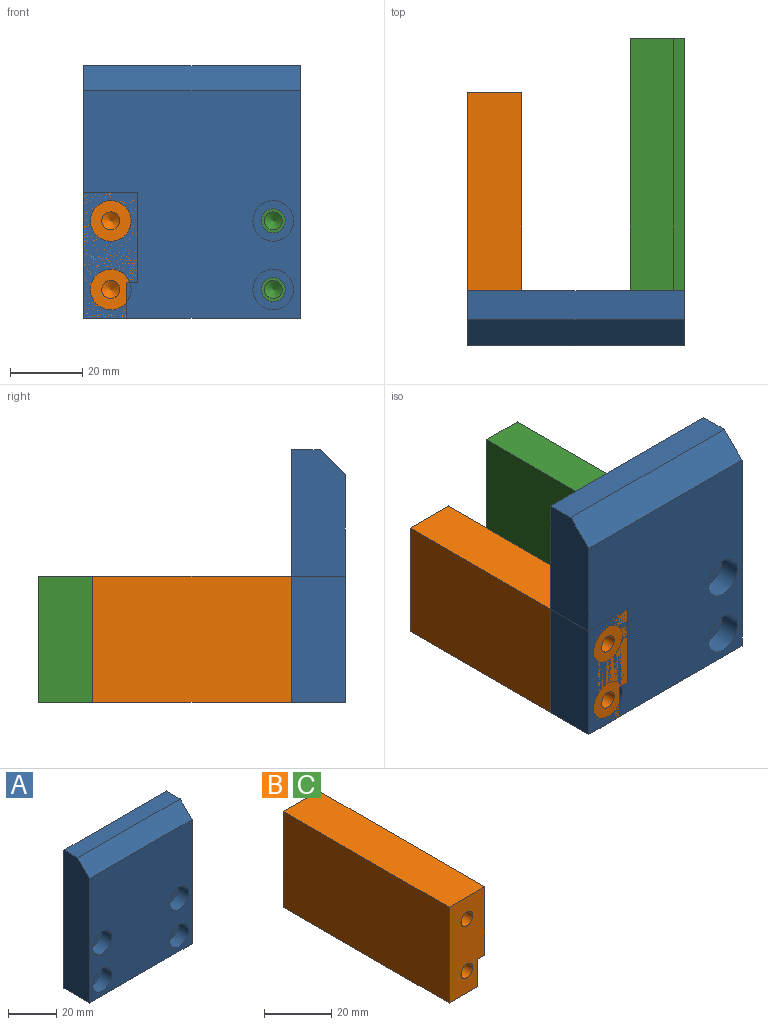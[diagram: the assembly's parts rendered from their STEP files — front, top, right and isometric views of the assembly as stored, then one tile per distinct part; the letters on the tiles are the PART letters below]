
ASSEMBLY  parts=3 mates=4
PART A: 19 faces, bbox 60x15x70 mm
  f0: plane 70x15mm, normal (-1,0,0), area 1025.5mm2, adj f1,f3,f4,f5,f6
  f1: plane 60x15mm, normal (0,0,-1), area 900mm2, adj f0,f2,f4,f5
  f2: plane 70x15mm, normal (1,0,0), area 1025.5mm2, adj f1,f3,f4,f5,f6
  f3: plane 60x8mm, normal (0,0,1), area 480mm2, adj f0,f2,f4,f6
  f4: plane 70x60mm, normal (0,1,0), area 4063.2mm2, adj f0,f1,f2,f3,f7,f10,f13,f16
  f5: plane 63x60mm, normal (0,-1,0), area 3382.4mm2, adj f0,f1,f2,f6,f9,f12,f15,f18
  f6: plane 60x7mm, normal (0,-0.71,0.71), area 594mm2, adj f0,f2,f3,f5
  f7: cylinder r=3.3mm len=9mm, axis (0,-1,0), area 186.6mm2, adj f4,f8
  f8: plane 11.25x11.25mm, normal (0,-1,0), area 65.2mm2, adj f7,f9
  f9: cylinder r=5.62mm len=11.25mm, axis (0,-1,0), area 212.1mm2, adj f5,f8
  f10: cylinder r=3.3mm len=9mm, axis (0,-1,0), area 186.6mm2, adj f4,f11
  f11: plane 11.25x11.25mm, normal (0,-1,0), area 65.2mm2, adj f10,f12
  f12: cylinder r=5.62mm len=11.25mm, axis (0,-1,0), area 212.1mm2, adj f5,f11
  f13: cylinder r=3.3mm len=9mm, axis (0,-1,0), area 186.6mm2, adj f4,f14
  f14: plane 11.25x11.25mm, normal (0,-1,0), area 65.2mm2, adj f13,f15
  f15: cylinder r=5.62mm len=11.25mm, axis (0,-1,0), area 212.1mm2, adj f5,f14
  f16: cylinder r=3.3mm len=9mm, axis (0,-1,0), area 186.6mm2, adj f4,f17
  f17: plane 11.25x11.25mm, normal (0,-1,0), area 65.2mm2, adj f16,f18
  f18: cylinder r=5.62mm len=11.25mm, axis (0,-1,0), area 212.1mm2, adj f5,f17
PART B: 16 faces, bbox 15x70x35 mm
  f0: plane 70x35mm, normal (-1,0,0), area 2450mm2, adj f1,f5,f6,f7
  f1: plane 70x12mm, normal (0,0,-1), area 840mm2, adj f0,f2,f6,f7
  f2: plane 70x10mm, normal (1,0,0), area 700mm2, adj f1,f3,f6,f7
  f3: plane 70x3mm, normal (0,0,-1), area 210mm2, adj f2,f4,f6,f7
  f4: plane 70x25mm, normal (1,0,0), area 1750mm2, adj f3,f5,f6,f7
  f5: plane 70x15mm, normal (0,0,1), area 1050mm2, adj f0,f4,f6,f7
  f6: plane 35x15mm, normal (0,1,0), area 455.7mm2, adj f0,f1,f2,f3,f4,f5,f13,f15
  f7: plane 35x15mm, normal (0,-1,0), area 455.7mm2, adj f0,f1,f2,f3,f4,f5,f9,f11
  f8: cone r=0mm half-angle=59deg, axis (0,-1,0), area 22.9mm2, adj f9
  f9: cylinder r=2.5mm len=15mm, axis (0,-1,0), area 235.6mm2, adj f7,f8
  f10: cone r=0mm half-angle=59deg, axis (0,-1,0), area 22.9mm2, adj f11
  f11: cylinder r=2.5mm len=15mm, axis (0,-1,0), area 235.6mm2, adj f7,f10
  f12: cone r=0mm half-angle=59deg, axis (0,1,0), area 22.9mm2, adj f13
  f13: cylinder r=2.5mm len=15mm, axis (0,1,0), area 235.6mm2, adj f6,f12
  f14: cone r=0mm half-angle=59deg, axis (0,1,0), area 22.9mm2, adj f15
  f15: cylinder r=2.5mm len=15mm, axis (0,1,0), area 235.6mm2, adj f6,f14
PART C: same geometry as B
PLACE A t=(-75.77,-115.09,-54.46)mm
PLACE B t=(-75.77,-115.09,-54.46)mm
PLACE C rot(axis=(1,0,0),180deg) t=(-30.77,-30.09,-19.46)mm
MATE planar A.f5 <-> B.f7  axis (0,-1,0) through (-45.77,-115.09,-21.31)mm
MATE cylindrical C.f10 <-> A.f16  axis (0,1,0) through (-23.27,-30.09,-27.46)mm
MATE planar C.f6 <-> A.f4  axis (0,-1,0) through (-23.67,-100.09,-37.78)mm
MATE cylindrical B.f8 <-> A.f7  axis (0,-1,0) through (-68.27,-115.09,-27.46)mm
